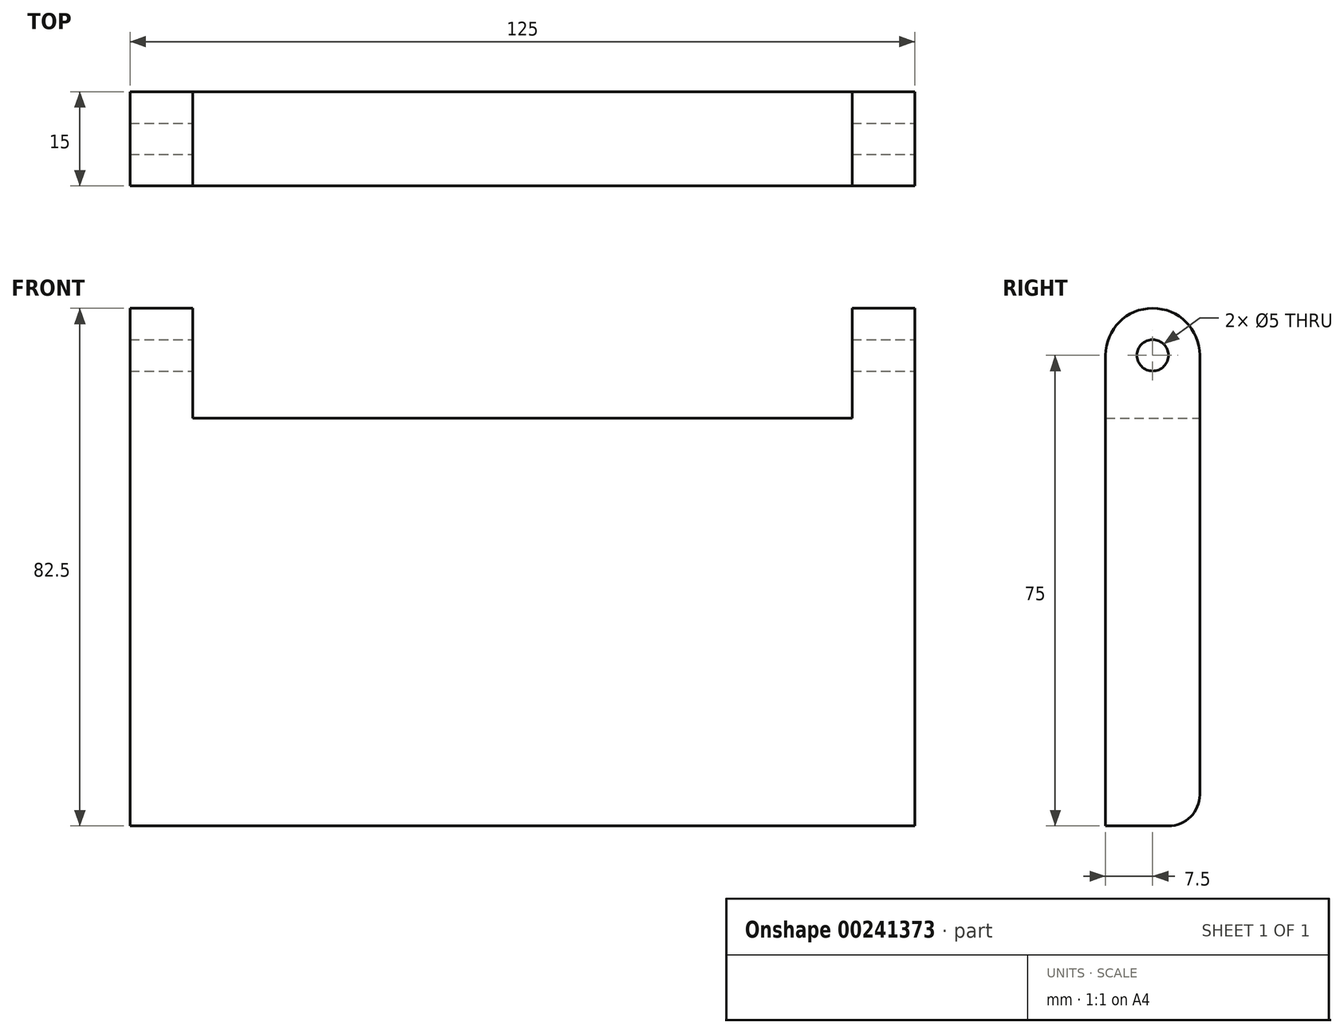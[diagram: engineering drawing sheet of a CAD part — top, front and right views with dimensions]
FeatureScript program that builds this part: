
annotation { "Feature Type Name" : "Feature", "Feature Type Description" : "" }
export const myFeature = defineFeature(function(context is Context, id is Id, definition is map)
    precondition{}
    {
        {
            var Q0;
            Q0=qCreatedBy(makeId("Front.planeOp"),FACE);
            var sketch = newSketch(context, id + "F0", { "sketchPlane" : qUnion([Q0])});
            skLineSegment(sketch, "E0.top", {"start": v(-62.5, -41.25) * mm, "end": v(62.5, -41.25) * mm});
            skLineSegment(sketch, "E0.left", {"start": v(-62.5, 41.25) * mm, "end": v(-62.5, -41.25) * mm});
            skLineSegment(sketch, "E0.right", {"start": v(62.5, 41.25) * mm, "end": v(62.5, -41.25) * mm});
            skPoint(sketch, "E0.middle", {"position": v(0, 0) * mm});
            skLineSegment(sketch, "E1.bottom", {"start": v(-62.5, 41.25) * mm, "end": v(-52.5, 41.25) * mm});
            skLineSegment(sketch, "E1.left", {"start": v(-62.5, 41.25) * mm, "end": v(-62.5, 23.75) * mm});
            skLineSegment(sketch, "E1.right", {"start": v(-52.5, 41.25) * mm, "end": v(-52.5, 23.75) * mm});
            skLineSegment(sketch, "E2.bottom", {"start": v(62.5, 41.25) * mm, "end": v(52.5, 41.25) * mm});
            skLineSegment(sketch, "E2.left", {"start": v(62.5, 41.25) * mm, "end": v(62.5, 23.75) * mm});
            skLineSegment(sketch, "E2.right", {"start": v(52.5, 41.25) * mm, "end": v(52.5, 23.75) * mm});
            skLineSegment(sketch, "E3", {"start": v(-52.5, 23.75) * mm, "end": v(52.5, 23.75) * mm});
            skSolve(sketch);
        }
        {
            var Q0;
            Q0 = qSketchRegion(id + "F0", true);
            extrude(context, id + "F1", {"entities" : qUnion([Q0]), "depth" : 15 * mm});
        }
        {
            var Q0;
            Q0=makeQuery(id+"F1.opExtrude","SWEPT_FACE",FACE,{"disambiguationData":[OSD([sQuery(id+"F0.wireOp",EDGE,"E0.right"),sQuery(id+"F0.wireOp",EDGE,"E2.left")])]});
            var sketch = newSketch(context, id + "F2", { "sketchPlane" : qUnion([Q0])});
            skCircle(sketch, "E4", {"center": v(-7.5, 33.75) * mm, "radius": 2.5 * mm});
            skPoint(sketch, "E4.centerSnap0", {"position": v(-7.5, 41.25) * mm});
            skSolve(sketch);
        }
        {
            var Q0;
            Q0 = qSketchRegion(id + "F2", true);
            extrude(context, id + "F3", {"entities" : qUnion([Q0]), "operationType" : NewBodyOperationType.REMOVE, "endBound" : BoundingType.THROUGH_ALL, "oppositeDirection" : true, "depth" : 25 * mm});
        }
        {
            var Q0;
            Q0=makeQuery(id+"F1.opExtrude","CAP_EDGE",EDGE,{"disambiguationData":[OSD([sQuery(id+"F0.wireOp",EDGE,"E2.bottom")])],"isStart":true});
            var Q1;
            Q1=makeQuery(id+"F1.opExtrude","CAP_EDGE",EDGE,{"disambiguationData":[OSD([sQuery(id+"F0.wireOp",EDGE,"E2.bottom")])],"isStart":false});
            var Q2;
            Q2=makeQuery(id+"F1.opExtrude","CAP_EDGE",EDGE,{"disambiguationData":[OSD([sQuery(id+"F0.wireOp",EDGE,"E1.bottom")])],"isStart":false});
            var Q3;
            Q3=makeQuery(id+"F1.opExtrude","CAP_EDGE",EDGE,{"disambiguationData":[OSD([sQuery(id+"F0.wireOp",EDGE,"E1.bottom")])],"isStart":true});
            fillet(context, id + "F4", {"entities" : qUnion([Q0, Q1, Q2, Q3]), "radius" : 7.5 * mm, "allowEdgeOverflow" : false});
        }
        {
            var Q0;
            Q0=makeQuery(id+"F1.opExtrude","CAP_EDGE",EDGE,{"disambiguationData":[OSD([sQuery(id+"F0.wireOp",EDGE,"E0.top")])],"isStart":true});
            fillet(context, id + "F5", {"entities" : qUnion([Q0]), "radius" : 5 * mm, "tangentPropagation" : true, "allowEdgeOverflow" : false});
        }
    });
